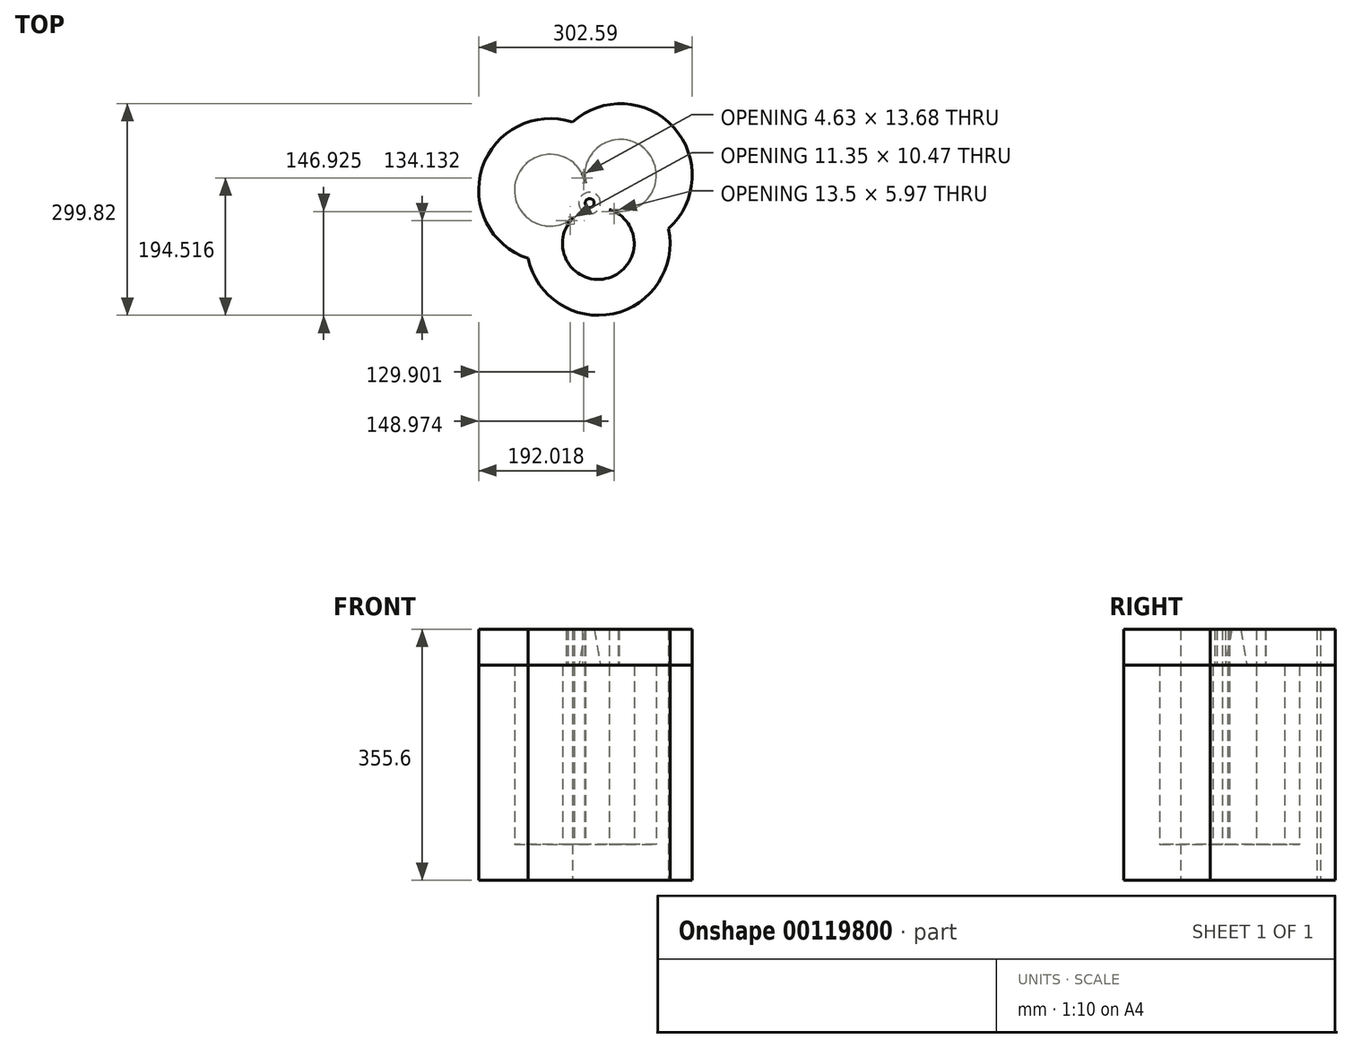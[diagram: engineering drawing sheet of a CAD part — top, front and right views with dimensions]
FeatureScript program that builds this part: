
annotation { "Feature Type Name" : "Feature", "Feature Type Description" : "" }
export const myFeature = defineFeature(function(context is Context, id is Id, definition is map)
    precondition{}
    {
        {
            var Q0;
            Q0=qCreatedBy(makeId("Top.planeOp"),FACE);
            var sketch = newSketch(context, id + "F0", { "sketchPlane" : qUnion([Q0])});
            skCircle(sketch, "E0", {"center": v(-67.95, 22.21) * mm, "radius": 50.8 * mm});
            skCircle(sketch, "E1", {"center": v(31.44, 43.3) * mm, "radius": 50.8 * mm});
            skCircle(sketch, "E2", {"center": v(0, -53.32) * mm, "radius": 50.8 * mm});
            skSolve(sketch);
        }
        {
            var Q0;
            Q0 = qSketchRegion(id + "F0", true);
            extrude(context, id + "F1", {"entities" : qUnion([Q0]), "depth" : 254 * mm});
        }
        {
            var Q0;
            Q0=makeQuery(id+"F1.opExtrude","CAP_FACE",FACE,{"disambiguationData":[OSD([sQuery(id+"F0.wireOp",EDGE,"E0"),sQuery(id+"F0.wireOp",EDGE,"E1"),sQuery(id+"F0.wireOp",EDGE,"E2")])],"isStart":false});
            shell(context, id + "F2", {"entities" : qUnion([Q0]), "thickness" : 50.8 * mm, "oppositeDirection" : true});
        }
        {
            var Q0;
            Q0=makeQuery(id+"F1.opExtrude","CAP_FACE",FACE,{"disambiguationData":[OSD([sQuery(id+"F0.wireOp",EDGE,"E0"),sQuery(id+"F0.wireOp",EDGE,"E1"),sQuery(id+"F0.wireOp",EDGE,"E2")])],"isStart":false});
            var sketch = newSketch(context, id + "F3", { "sketchPlane" : qUnion([Q0])});
            skCircle(sketch, "E3", {"center": v(-67.95, 22.21) * mm, "radius": 101.6 * mm});
            skCircle(sketch, "E4", {"center": v(0, -53.32) * mm, "radius": 101.6 * mm});
            skCircle(sketch, "E5", {"center": v(31.44, 43.3) * mm, "radius": 101.6 * mm});
            skSolve(sketch);
        }
        {
            var Q0;
            Q0 = qSketchRegion(id + "F3", true);
            var Q1;
            {var subQ7=sQuery(id+"F3.wireOp",EDGE,"E3");var subQ10=sQuery(id+"F3.wireOp",EDGE,"E5");var subQ18=makeQuery(id+"F3.imprint","INTERSECT",VERTEX,{"disambiguationData":[OD(1.0)],"derivedFrom":[subQ7,subQ10]});Q1=makeQuery(id+"F3.imprint","IMPRINT",FACE,{"disambiguationData":[TD([[makeQuery(id+"F3.imprint","IMPRINT",EDGE,{"disambiguationData":[TD([[subQ18,-1.0]])],"derivedFrom":subQ7}),1.0]])]});}
            extrude(context, id + "F4", {"entities" : qUnion([Q0, Q1]), "depth" : 50.8 * mm});
        }
        {
            var Q0;
            Q0=makeQuery(id+"F4.opExtrude","CAP_FACE",FACE,{"disambiguationData":[OSD([sQuery(id+"F0.wireOp",EDGE,"E0"),sQuery(id+"F0.wireOp",EDGE,"E1"),sQuery(id+"F0.wireOp",EDGE,"E2"),sQuery(id+"F3.wireOp",EDGE,"E3"),sQuery(id+"F3.wireOp",EDGE,"E4"),sQuery(id+"F3.wireOp",EDGE,"E5")])],"isStart":false});
            var sketch = newSketch(context, id + "F5", { "sketchPlane" : qUnion([Q0])});
            skCircle(sketch, "E6", {"center": v(-12.17, 4.06) * mm, "radius": 6.35 * mm});
            skSolve(sketch);
        }
        {
            var Q0;
            Q0=makeQuery(id+"F5.imprint","IMPRINT",FACE,{"disambiguationData":[TD([[makeQuery(id+"F5.imprint","IMPRINT",EDGE,{"derivedFrom":sQuery(id+"F5.wireOp",EDGE,"E6")}),1.0]])]});
            extrude(context, id + "F6", {"entities" : qUnion([Q0]), "operationType" : NewBodyOperationType.REMOVE, "oppositeDirection" : true, "depth" : 63.5 * mm, "hasDraft" : true, "draftAngle" : 10 * degree});
        }
    });
